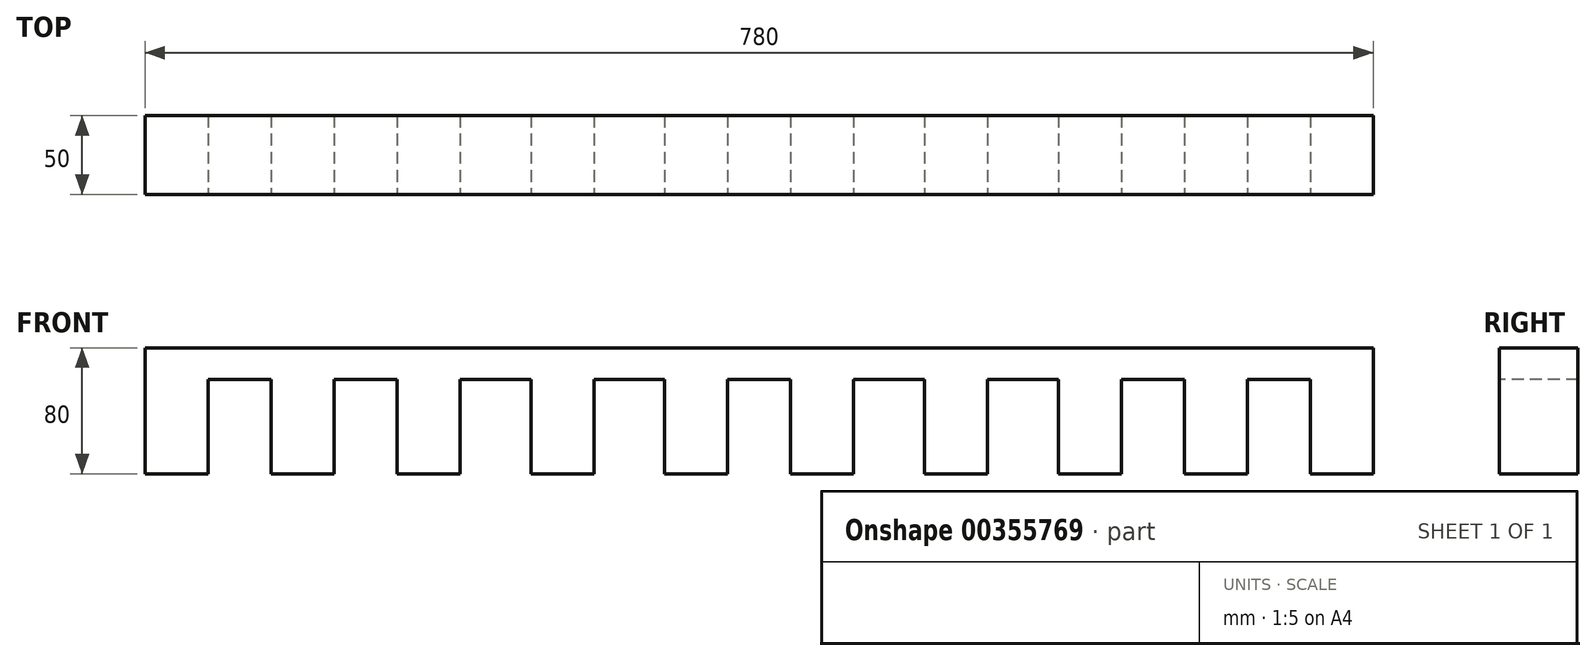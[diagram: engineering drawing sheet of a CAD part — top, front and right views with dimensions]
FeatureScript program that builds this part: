
annotation { "Feature Type Name" : "Feature", "Feature Type Description" : "" }
export const myFeature = defineFeature(function(context is Context, id is Id, definition is map)
    precondition{}
    {
        {
            var Q0;
            Q0=qCreatedBy(makeId("Front.planeOp"),FACE);
            var sketch = newSketch(context, id + "F0", { "sketchPlane" : qUnion([Q0])});
            skLineSegment(sketch, "E0.bottom", {"start": v(-404.78, 0) * mm, "end": v(375.22, 0) * mm});
            skLineSegment(sketch, "E0.top", {"start": v(-404.78, -80) * mm, "end": v(375.22, -80) * mm});
            skLineSegment(sketch, "E0.left", {"start": v(-404.78, 0) * mm, "end": v(-404.78, -80) * mm});
            skLineSegment(sketch, "E0.right", {"start": v(375.22, 0) * mm, "end": v(375.22, -80) * mm});
            skSolve(sketch);
        }
        {
            var Q0;
            Q0=makeQuery(id+"F0.imprint","IMPRINT",FACE,{"disambiguationData":[TD([[makeQuery(id+"F0.imprint","IMPRINT",EDGE,{"derivedFrom":sQuery(id+"F0.wireOp",EDGE,"E0.bottom")}),-1.0]])]});
            extrude(context, id + "F1", {"entities" : qUnion([Q0]), "depth" : 50 * mm});
        }
        {
            var Q0;
            Q0=makeQuery(id+"F1.opExtrude","CAP_FACE",FACE,{"disambiguationData":[OSD([sQuery(id+"F0.wireOp",EDGE,"E0.bottom"),sQuery(id+"F0.wireOp",EDGE,"E0.top"),sQuery(id+"F0.wireOp",EDGE,"E0.left"),sQuery(id+"F0.wireOp",EDGE,"E0.right")])],"isStart":false});
            var sketch = newSketch(context, id + "F2", { "sketchPlane" : qUnion([Q0])});
            skLineSegment(sketch, "E1.bottom", {"start": v(-364.78, -80) * mm, "end": v(-324.78, -80) * mm});
            skLineSegment(sketch, "E1.top", {"start": v(-364.78, -20) * mm, "end": v(-324.78, -20) * mm});
            skLineSegment(sketch, "E1.left", {"start": v(-364.78, -80) * mm, "end": v(-364.78, -20) * mm});
            skLineSegment(sketch, "E1.right", {"start": v(-324.78, -80) * mm, "end": v(-324.78, -20) * mm});
            skLineSegment(sketch, "E2.bottom", {"start": v(-284.78, -80) * mm, "end": v(-244.78, -80) * mm});
            skLineSegment(sketch, "E2.top", {"start": v(-284.78, -20) * mm, "end": v(-244.78, -20) * mm});
            skLineSegment(sketch, "E2.left", {"start": v(-284.78, -80) * mm, "end": v(-284.78, -20) * mm});
            skLineSegment(sketch, "E2.right", {"start": v(-244.78, -80) * mm, "end": v(-244.78, -20) * mm});
            skLineSegment(sketch, "E3.bottom", {"start": v(-204.78, -80) * mm, "end": v(-159.78, -80) * mm});
            skLineSegment(sketch, "E3.top", {"start": v(-204.78, -20) * mm, "end": v(-159.78, -20) * mm});
            skLineSegment(sketch, "E3.left", {"start": v(-204.78, -80) * mm, "end": v(-204.78, -20) * mm});
            skLineSegment(sketch, "E3.right", {"start": v(-159.78, -80) * mm, "end": v(-159.78, -20) * mm});
            skPoint(sketch, "E4.oppositeSnap0", {"position": v(-182.28, -20) * mm});
            skLineSegment(sketch, "E4.bottom", {"start": v(-119.78, -80) * mm, "end": v(-74.78, -80) * mm});
            skLineSegment(sketch, "E4.top", {"start": v(-119.78, -20) * mm, "end": v(-74.78, -20) * mm});
            skLineSegment(sketch, "E4.left", {"start": v(-119.78, -80) * mm, "end": v(-119.78, -20) * mm});
            skLineSegment(sketch, "E4.right", {"start": v(-74.78, -80) * mm, "end": v(-74.78, -20) * mm});
            skLineSegment(sketch, "E5.bottom", {"start": v(-34.78, -80) * mm, "end": v(5.22, -80) * mm});
            skLineSegment(sketch, "E5.top", {"start": v(-34.78, -20) * mm, "end": v(5.22, -20) * mm});
            skLineSegment(sketch, "E5.left", {"start": v(-34.78, -80) * mm, "end": v(-34.78, -20) * mm});
            skLineSegment(sketch, "E5.right", {"start": v(5.22, -80) * mm, "end": v(5.22, -20) * mm});
            skLineSegment(sketch, "E6.bottom", {"start": v(45.22, -80) * mm, "end": v(90.22, -80) * mm});
            skLineSegment(sketch, "E6.top", {"start": v(45.22, -20) * mm, "end": v(90.22, -20) * mm});
            skLineSegment(sketch, "E6.left", {"start": v(45.22, -80) * mm, "end": v(45.22, -20) * mm});
            skLineSegment(sketch, "E6.right", {"start": v(90.22, -80) * mm, "end": v(90.22, -20) * mm});
            skLineSegment(sketch, "E7.bottom", {"start": v(130.22, -80) * mm, "end": v(175.22, -80) * mm});
            skLineSegment(sketch, "E7.top", {"start": v(130.22, -20) * mm, "end": v(175.22, -20) * mm});
            skLineSegment(sketch, "E7.left", {"start": v(130.22, -80) * mm, "end": v(130.22, -20) * mm});
            skLineSegment(sketch, "E7.right", {"start": v(175.22, -80) * mm, "end": v(175.22, -20) * mm});
            skLineSegment(sketch, "E8.bottom", {"start": v(215.22, -80) * mm, "end": v(255.22, -80) * mm});
            skLineSegment(sketch, "E8.top", {"start": v(215.22, -20) * mm, "end": v(255.22, -20) * mm});
            skLineSegment(sketch, "E8.left", {"start": v(215.22, -80) * mm, "end": v(215.22, -20) * mm});
            skLineSegment(sketch, "E8.right", {"start": v(255.22, -80) * mm, "end": v(255.22, -20) * mm});
            skLineSegment(sketch, "E9.bottom", {"start": v(295.22, -80) * mm, "end": v(335.22, -80) * mm});
            skLineSegment(sketch, "E9.top", {"start": v(295.22, -20) * mm, "end": v(335.22, -20) * mm});
            skLineSegment(sketch, "E9.left", {"start": v(295.22, -80) * mm, "end": v(295.22, -20) * mm});
            skLineSegment(sketch, "E9.right", {"start": v(335.22, -80) * mm, "end": v(335.22, -20) * mm});
            skSolve(sketch);
        }
        {
            var Q0;
            Q0 = qSketchRegion(id + "F2", true);
            extrude(context, id + "F3", {"entities" : qUnion([Q0]), "operationType" : NewBodyOperationType.REMOVE, "oppositeDirection" : true, "depth" : 50 * mm});
        }
    });
